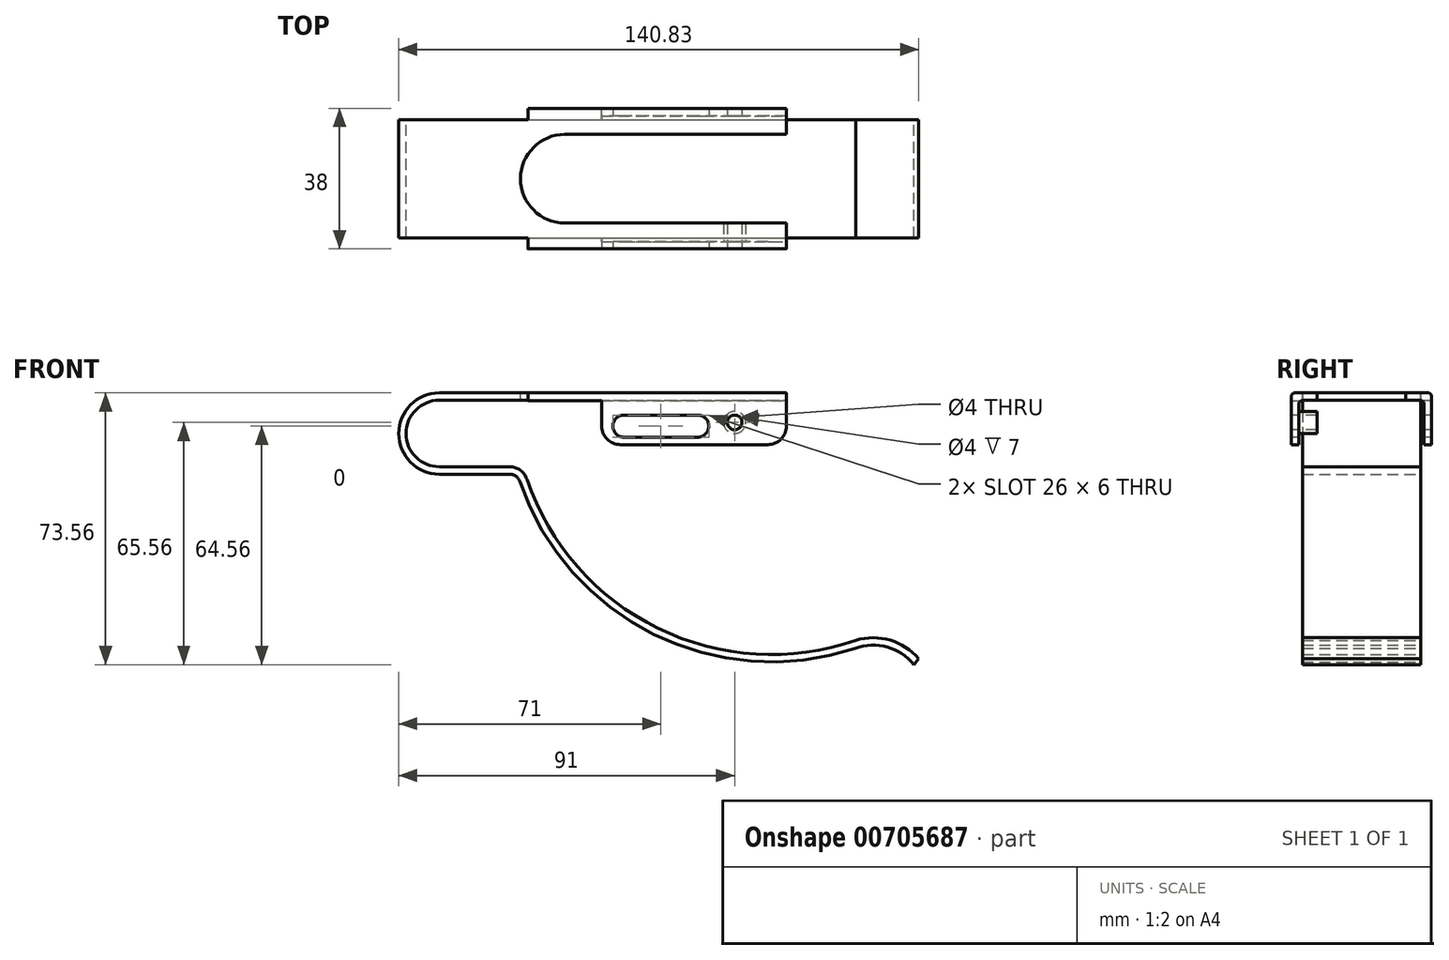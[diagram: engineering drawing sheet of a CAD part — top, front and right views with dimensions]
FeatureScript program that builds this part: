
annotation { "Feature Type Name" : "Feature", "Feature Type Description" : "" }
export const myFeature = defineFeature(function(context is Context, id is Id, definition is map)
    precondition{}
    {
        {
            var Q0;
            Q0=qCreatedBy(makeId("Front.planeOp"),FACE);
            var sketch = newSketch(context, id + "F0", { "sketchPlane" : qUnion([Q0])});
            skArc(sketch, "E0", {"start": v(0, 9) * mm, "mid": v(-9, 0) * mm, "end": v(0, -9) * mm});
            skLineSegment(sketch, "E1", {"start": v(0, 9) * mm, "end": v(94, 9) * mm});
            skLineSegment(sketch, "E2", {"start": v(0, -9) * mm, "end": v(19, -9) * mm});
            skArc(sketch, "E3", {"start": v(23.73, -12.39) * mm, "mid": v(59.23, -52.7) * mm, "end": v(112.85, -56) * mm});
            skArc(sketch, "E4", {"start": v(129.83, -61) * mm, "mid": v(122.1, -55.94) * mm, "end": v(112.85, -56) * mm});
            skPoint(sketch, "E5.visualSharp", {"position": v(22.67, -9) * mm});
            skArc(sketch, "E5.filletArc", {"start": v(23.73, -12.39) * mm, "mid": v(21.91, -9.93) * mm, "end": v(19, -9) * mm});
            skLineSegment(sketch, "E6.0", {"start": v(0, 11) * mm, "end": v(94, 11) * mm});
            skArc(sketch, "E6.1", {"start": v(0, 11) * mm, "mid": v(-11, 0) * mm, "end": v(0, -11) * mm});
            skArc(sketch, "E6.2", {"start": v(128.52, -62.56) * mm, "mid": v(121.32, -57.8) * mm, "end": v(112.7, -58.16) * mm});
            skArc(sketch, "E6.3", {"start": v(21.84, -13.03) * mm, "mid": v(57.97, -54.32) * mm, "end": v(112.7, -58.16) * mm});
            skArc(sketch, "E6.4", {"start": v(21.84, -13.03) * mm, "mid": v(20.75, -11.56) * mm, "end": v(19, -11) * mm});
            skLineSegment(sketch, "E6.5", {"start": v(0, -11) * mm, "end": v(19, -11) * mm});
            skLineSegment(sketch, "E7", {"start": v(128.52, -62.56) * mm, "end": v(129.83, -61) * mm});
            skLineSegment(sketch, "E8", {"start": v(94, 11) * mm, "end": v(94, 9) * mm});
            skLineSegment(sketch, "E9", {"start": v(129.83, -61) * mm, "end": v(156.97, -61) * mm, "construction": true});
            skSolve(sketch);
        }
        {
            var Q0;
            Q0 = qSketchRegion(id + "F0", true);
            extrude(context, id + "F1", {"entities" : qUnion([Q0]), "depth" : 16 * mm, "offsetDistance" : 25 * mm});
        }
        {
            var Q0;
            Q0=makeQuery(id+"F1.opExtrude","SWEPT_FACE",FACE,{"disambiguationData":[OSD([sQuery(id+"F0.wireOp",EDGE,"E6.0")])]});
            var sketch = newSketch(context, id + "F2", { "sketchPlane" : qUnion([Q0])});
            skLineSegment(sketch, "E10.bottom", {"start": v(24, -19) * mm, "end": v(94, -19) * mm});
            skLineSegment(sketch, "E10.top", {"start": v(24, -16) * mm, "end": v(94, -16) * mm});
            skLineSegment(sketch, "E10.left", {"start": v(24, -19) * mm, "end": v(24, -16) * mm});
            skLineSegment(sketch, "E10.right", {"start": v(94, -19) * mm, "end": v(94, -16) * mm});
            skSolve(sketch);
        }
        {
            var Q0;
            Q0=makeQuery(id+"F2.imprint","IMPRINT",FACE,{"disambiguationData":[TD([[makeQuery(id+"F2.imprint","IMPRINT",EDGE,{"derivedFrom":sQuery(id+"F2.wireOp",EDGE,"E10.bottom")}),1.0]])]});
            extrude(context, id + "F3", {"entities" : qUnion([Q0]), "operationType" : NewBodyOperationType.ADD, "oppositeDirection" : true, "depth" : 2.1 * mm, "offsetDistance" : 25 * mm});
        }
        {
            var Q0;
            Q0=makeQuery(id+"F3.opExtrude","SWEPT_FACE",FACE,{"disambiguationData":[OSD([sQuery(id+"F2.wireOp",EDGE,"E10.bottom")])]});
            var sketch = newSketch(context, id + "F4", { "sketchPlane" : qUnion([Q0])});
            skLineSegment(sketch, "E11.bottom", {"start": v(94, 11) * mm, "end": v(44, 11) * mm});
            skLineSegment(sketch, "E11.top", {"start": v(94, -3) * mm, "end": v(44, -3) * mm});
            skLineSegment(sketch, "E11.left", {"start": v(94, 11) * mm, "end": v(94, -3) * mm});
            skLineSegment(sketch, "E11.right", {"start": v(44, 11) * mm, "end": v(44, -3) * mm});
            skSolve(sketch);
        }
        {
            var Q0;
            Q0 = qSketchRegion(id + "F4", true);
            extrude(context, id + "F5", {"entities" : qUnion([Q0]), "operationType" : NewBodyOperationType.ADD, "oppositeDirection" : true, "depth" : 2 * mm, "offsetDistance" : 25 * mm});
        }
        {
            var Q0;
            Q0=makeQuery(id+"F3.opExtrude","CAP_EDGE",EDGE,{"disambiguationData":[OSD([sQuery(id+"F2.wireOp",EDGE,"E10.bottom")])],"isStart":true});
            var Q1;
            Q1=makeQuery(id+"F5.boolean.opBoolean","INTERSECT",EDGE,{"derivedFrom":[makeQuery(id+"F3.opExtrude","CAP_FACE",FACE,{"disambiguationData":[OSD([sQuery(id+"F2.wireOp",EDGE,"E10.bottom"),sQuery(id+"F2.wireOp",EDGE,"E10.top"),sQuery(id+"F2.wireOp",EDGE,"E10.left"),sQuery(id+"F2.wireOp",EDGE,"E10.right")])],"isStart":false}),makeQuery(id+"F5.opExtrude","CAP_FACE",FACE,{"disambiguationData":[OSD([sQuery(id+"F4.wireOp",EDGE,"E11.bottom"),sQuery(id+"F4.wireOp",EDGE,"E11.top"),sQuery(id+"F4.wireOp",EDGE,"E11.left"),sQuery(id+"F4.wireOp",EDGE,"E11.right")])],"isStart":false})]});
            fillet(context, id + "F6", {"entities" : qUnion([Q0, Q1]), "radius" : 1 * mm, "allowEdgeOverflow" : false});
        }
        {
            var Q0;
            Q0=makeQuery(id+"F1.opExtrude","SWEPT_BODY",BODY,{"disambiguationData":[OSD([sQuery(id+"F0.wireOp",EDGE,"E0"),sQuery(id+"F0.wireOp",EDGE,"E1"),sQuery(id+"F0.wireOp",EDGE,"E2"),sQuery(id+"F0.wireOp",EDGE,"E3"),sQuery(id+"F0.wireOp",EDGE,"E4"),sQuery(id+"F0.wireOp",EDGE,"E5.filletArc"),sQuery(id+"F0.wireOp",EDGE,"E6.0"),sQuery(id+"F0.wireOp",EDGE,"E6.1"),sQuery(id+"F0.wireOp",EDGE,"E6.2"),sQuery(id+"F0.wireOp",EDGE,"E6.3"),sQuery(id+"F0.wireOp",EDGE,"E6.4"),sQuery(id+"F0.wireOp",EDGE,"E6.5"),sQuery(id+"F0.wireOp",EDGE,"E7"),sQuery(id+"F0.wireOp",EDGE,"E8")])]});
            var Q1;
            Q1=qCreatedBy(makeId("Front.planeOp"),FACE);
            mirror(context, id + "F7", {"operationType" : NewBodyOperationType.ADD, "entities" : qUnion([Q0]), "mirrorPlane" : qUnion([Q1])});
        }
        {
            var Q0;
            {var subQ0=makeQuery(id+"F3.boolean.opBoolean","MERGE",FACE,{"derivedFrom":[makeQuery(id+"F1.opExtrude","SWEPT_FACE",FACE,{"disambiguationData":[OSD([sQuery(id+"F0.wireOp",EDGE,"E6.0")])]}),makeQuery(id+"F3.opExtrude","CAP_FACE",FACE,{"disambiguationData":[OSD([sQuery(id+"F2.wireOp",EDGE,"E10.bottom"),sQuery(id+"F2.wireOp",EDGE,"E10.top"),sQuery(id+"F2.wireOp",EDGE,"E10.left"),sQuery(id+"F2.wireOp",EDGE,"E10.right")])],"isStart":true})]});Q0=makeQuery(id+"F7.boolean.opBoolean","MERGE",FACE,{"derivedFrom":[subQ0,makeQuery(id+"F7.opPattern","COPY",FACE,{"derivedFrom":subQ0,"instanceName":"1"})]});}
            var sketch = newSketch(context, id + "F8", { "sketchPlane" : qUnion([Q0])});
            skArc(sketch, "E12", {"start": v(34, 12) * mm, "mid": v(22, 0) * mm, "end": v(34, -12) * mm});
            skLineSegment(sketch, "E13", {"start": v(34, 12) * mm, "end": v(94, 12) * mm});
            skLineSegment(sketch, "E14", {"start": v(34, -12) * mm, "end": v(94, -12) * mm});
            skLineSegment(sketch, "E15", {"start": v(94, 12) * mm, "end": v(94, -12) * mm});
            skSolve(sketch);
        }
        {
            var Q0;
            Q0 = qSketchRegion(id + "F8", true);
            extrude(context, id + "F9", {"entities" : qUnion([Q0]), "operationType" : NewBodyOperationType.REMOVE, "oppositeDirection" : true, "depth" : 2 * mm, "offsetDistance" : 25 * mm});
        }
        {
            var Q0;
            Q0=makeQuery(id+"F5.boolean.opBoolean","MERGE",FACE,{"derivedFrom":[makeQuery(id+"F3.opExtrude","SWEPT_FACE",FACE,{"disambiguationData":[OSD([sQuery(id+"F2.wireOp",EDGE,"E10.bottom")])]}),makeQuery(id+"F5.opExtrude","CAP_FACE",FACE,{"disambiguationData":[OSD([sQuery(id+"F4.wireOp",EDGE,"E11.bottom"),sQuery(id+"F4.wireOp",EDGE,"E11.top"),sQuery(id+"F4.wireOp",EDGE,"E11.left"),sQuery(id+"F4.wireOp",EDGE,"E11.right")])],"isStart":true})]});
            var sketch = newSketch(context, id + "F10", { "sketchPlane" : qUnion([Q0])});
            skLineSegment(sketch, "E16", {"start": v(50, 2) * mm, "end": v(70, 2) * mm});
            skArc(sketch, "E17.0.startCap", {"start": v(50, -1) * mm, "mid": v(47, 2) * mm, "end": v(50, 5) * mm});
            skArc(sketch, "E17.0.endCap", {"start": v(70, 5) * mm, "mid": v(73, 2) * mm, "end": v(70, -1) * mm});
            skLineSegment(sketch, "E17.0.left", {"start": v(50, 5) * mm, "end": v(70, 5) * mm});
            skLineSegment(sketch, "E17.0.right", {"start": v(50, -1) * mm, "end": v(70, -1) * mm});
            skSolve(sketch);
        }
        {
            var Q0;
            Q0 = qSketchRegion(id + "F10", true);
            extrude(context, id + "F11", {"entities" : qUnion([Q0]), "operationType" : NewBodyOperationType.REMOVE, "endBound" : BoundingType.THROUGH_ALL, "oppositeDirection" : true, "depth" : 25 * mm, "offsetDistance" : 25 * mm});
        }
        {
            var Q0;
            Q0=makeQuery(id+"F5.boolean.opBoolean","MERGE",FACE,{"derivedFrom":[makeQuery(id+"F3.opExtrude","SWEPT_FACE",FACE,{"disambiguationData":[OSD([sQuery(id+"F2.wireOp",EDGE,"E10.bottom")])]}),makeQuery(id+"F5.opExtrude","CAP_FACE",FACE,{"disambiguationData":[OSD([sQuery(id+"F4.wireOp",EDGE,"E11.bottom"),sQuery(id+"F4.wireOp",EDGE,"E11.top"),sQuery(id+"F4.wireOp",EDGE,"E11.left"),sQuery(id+"F4.wireOp",EDGE,"E11.right")])],"isStart":true})]});
            var sketch = newSketch(context, id + "F12", { "sketchPlane" : qUnion([Q0])});
            skPoint(sketch, "E18", {"position": v(80, 3) * mm});
            skSolve(sketch);
        }
        {
            var Q0;
            Q0=sQuery(id+"F12.wireOp",VERTEX,"E18");
            var Q1;
            Q1=makeQuery(id+"F1.opExtrude","SWEPT_BODY",BODY,{"disambiguationData":[OSD([sQuery(id+"F0.wireOp",EDGE,"E0"),sQuery(id+"F0.wireOp",EDGE,"E1"),sQuery(id+"F0.wireOp",EDGE,"E2"),sQuery(id+"F0.wireOp",EDGE,"E3"),sQuery(id+"F0.wireOp",EDGE,"E4"),sQuery(id+"F0.wireOp",EDGE,"E5.filletArc"),sQuery(id+"F0.wireOp",EDGE,"E6.0"),sQuery(id+"F0.wireOp",EDGE,"E6.1"),sQuery(id+"F0.wireOp",EDGE,"E6.2"),sQuery(id+"F0.wireOp",EDGE,"E6.3"),sQuery(id+"F0.wireOp",EDGE,"E6.4"),sQuery(id+"F0.wireOp",EDGE,"E6.5"),sQuery(id+"F0.wireOp",EDGE,"E7"),sQuery(id+"F0.wireOp",EDGE,"E8")])]});
            hole(context, id + "F13", {"style" : HoleStyle.SIMPLE, "endStyle" : HoleEndStyle.THROUGH, "holeDiameter" : 4 * mm, "majorDiameter" : 5 * mm, "isTappedThrough" : true, "tappedDepth" : 12 * mm, "tapClearance" : 3, "locations" : qUnion([Q0]), "scope" : qUnion([Q1])});
        }
        {
            var Q0;
            Q0=makeQuery(id+"F5.opExtrude","CAP_FACE",FACE,{"disambiguationData":[OSD([sQuery(id+"F4.wireOp",EDGE,"E11.bottom"),sQuery(id+"F4.wireOp",EDGE,"E11.top"),sQuery(id+"F4.wireOp",EDGE,"E11.left"),sQuery(id+"F4.wireOp",EDGE,"E11.right")])],"isStart":false});
            var sketch = newSketch(context, id + "F14", { "sketchPlane" : qUnion([Q0])});
            skCircle(sketch, "E19.0", {"center": v(-80, 3) * mm, "radius": 2 * mm});
            skCircle(sketch, "E20.0", {"center": v(-80, 3) * mm, "radius": 3 * mm});
            skSolve(sketch);
        }
        {
            var Q0;
            Q0=makeQuery(id+"F14.imprint","IMPRINT",FACE,{"disambiguationData":[TD([[makeQuery(id+"F14.imprint","IMPRINT",EDGE,{"derivedFrom":sQuery(id+"F14.wireOp",EDGE,"E19.0")}),-1.0]])]});
            extrude(context, id + "F15", {"entities" : qUnion([Q0]), "operationType" : NewBodyOperationType.ADD, "depth" : 5 * mm, "offsetDistance" : 25 * mm});
        }
        {
            var Q0;
            Q0=makeQuery(id+"F5.opExtrude","SWEPT_EDGE",EDGE,{"disambiguationData":[OSD([sQuery(id+"F4.wireOp",EDGE,"E11.top"),sQuery(id+"F4.wireOp",EDGE,"E11.left")])]});
            var Q1;
            Q1=makeQuery(id+"F7.opPattern","COPY",EDGE,{"derivedFrom":makeQuery(id+"F5.opExtrude","SWEPT_EDGE",EDGE,{"disambiguationData":[OSD([sQuery(id+"F4.wireOp",EDGE,"E11.top"),sQuery(id+"F4.wireOp",EDGE,"E11.left")])]}),"instanceName":"1"});
            var Q2;
            Q2=makeQuery(id+"F5.opExtrude","SWEPT_EDGE",EDGE,{"disambiguationData":[OSD([sQuery(id+"F4.wireOp",EDGE,"E11.top"),sQuery(id+"F4.wireOp",EDGE,"E11.right")])]});
            var Q3;
            Q3=makeQuery(id+"F7.opPattern","COPY",EDGE,{"derivedFrom":makeQuery(id+"F5.opExtrude","SWEPT_EDGE",EDGE,{"disambiguationData":[OSD([sQuery(id+"F4.wireOp",EDGE,"E11.top"),sQuery(id+"F4.wireOp",EDGE,"E11.right")])]}),"instanceName":"1"});
            fillet(context, id + "F16", {"entities" : qUnion([Q0, Q1, Q2, Q3]), "radius" : 5 * mm, "tangentPropagation" : true, "allowEdgeOverflow" : false});
        }
    });
